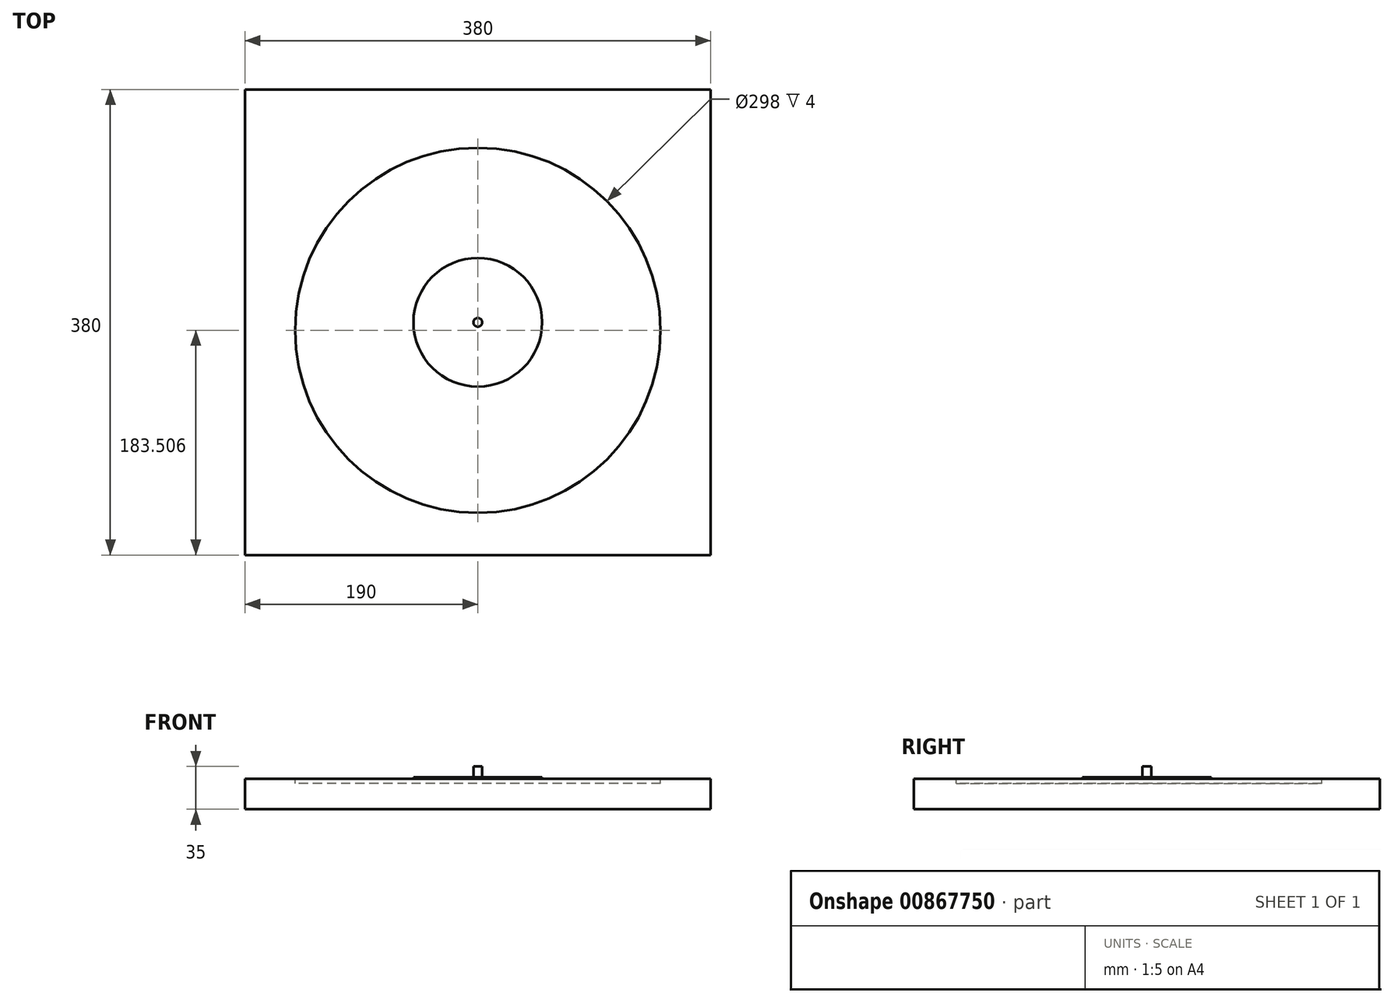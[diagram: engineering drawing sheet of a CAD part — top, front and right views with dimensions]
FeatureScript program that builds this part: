
annotation { "Feature Type Name" : "Feature", "Feature Type Description" : "" }
export const myFeature = defineFeature(function(context is Context, id is Id, definition is map)
    precondition{}
    {
        {
            var Q0;
            Q0=qCreatedBy(makeId("Top.planeOp"),FACE);
            var sketch = newSketch(context, id + "F0", { "sketchPlane" : qUnion([Q0])});
            skLineSegment(sketch, "E0.bottom", {"start": v(-190, 190) * mm, "end": v(190, 190) * mm});
            skLineSegment(sketch, "E0.top", {"start": v(-190, -190) * mm, "end": v(190, -190) * mm});
            skLineSegment(sketch, "E0.left", {"start": v(-190, 190) * mm, "end": v(-190, -190) * mm});
            skLineSegment(sketch, "E0.right", {"start": v(190, 190) * mm, "end": v(190, -190) * mm});
            skPoint(sketch, "E0.middle", {"position": v(0, 0) * mm});
            skSolve(sketch);
        }
        {
            var Q0;
            Q0=makeQuery(id+"F0.imprint","IMPRINT",FACE,{"disambiguationData":[TD([[makeQuery(id+"F0.imprint","IMPRINT",EDGE,{"derivedFrom":sQuery(id+"F0.wireOp",EDGE,"E0.bottom")}),-1.0]])]});
            extrude(context, id + "F1", {"entities" : qUnion([Q0]), "depth" : 25 * mm, "offsetDistance" : 25 * mm});
        }
        {
            var Q0;
            Q0=makeQuery(id+"F1.opExtrude","CAP_FACE",FACE,{"disambiguationData":[OSD([sQuery(id+"F0.wireOp",EDGE,"E0.bottom"),sQuery(id+"F0.wireOp",EDGE,"E0.top"),sQuery(id+"F0.wireOp",EDGE,"E0.left"),sQuery(id+"F0.wireOp",EDGE,"E0.right")])],"isStart":false});
            var sketch = newSketch(context, id + "F2", { "sketchPlane" : qUnion([Q0])});
            skCircle(sketch, "E1", {"center": v(0, -6.5) * mm, "radius": 149 * mm});
            skSolve(sketch);
        }
        {
            var Q0;
            Q0=makeQuery(id+"F2.imprint","IMPRINT",FACE,{"disambiguationData":[TD([[makeQuery(id+"F2.imprint","IMPRINT",EDGE,{"derivedFrom":sQuery(id+"F2.wireOp",EDGE,"E1")}),1.0]])]});
            extrude(context, id + "F3", {"entities" : qUnion([Q0]), "operationType" : NewBodyOperationType.REMOVE, "oppositeDirection" : true, "depth" : 4 * mm, "offsetDistance" : 25 * mm});
        }
        {
            var Q0;
            Q0=makeQuery(id+"F1.opExtrude","CAP_FACE",FACE,{"disambiguationData":[OSD([sQuery(id+"F0.wireOp",EDGE,"E0.bottom"),sQuery(id+"F0.wireOp",EDGE,"E0.top"),sQuery(id+"F0.wireOp",EDGE,"E0.left"),sQuery(id+"F0.wireOp",EDGE,"E0.right")])],"isStart":false});
            var sketch = newSketch(context, id + "F4", { "sketchPlane" : qUnion([Q0])});
            skCircle(sketch, "E2", {"center": v(0, 0) * mm, "radius": 52.5 * mm});
            skSolve(sketch);
        }
        {
            var Q0;
            Q0=makeQuery(id+"F4.imprint","IMPRINT",FACE,{"disambiguationData":[TD([[makeQuery(id+"F4.imprint","IMPRINT",EDGE,{"derivedFrom":sQuery(id+"F4.wireOp",EDGE,"E2")}),1.0]])]});
            extrude(context, id + "F5", {"entities" : qUnion([Q0]), "depth" : 1 * mm, "offsetDistance" : 25 * mm});
        }
        {
            var Q0;
            Q0=makeQuery(id+"F1.opExtrude","CAP_FACE",FACE,{"disambiguationData":[OSD([sQuery(id+"F0.wireOp",EDGE,"E0.bottom"),sQuery(id+"F0.wireOp",EDGE,"E0.top"),sQuery(id+"F0.wireOp",EDGE,"E0.left"),sQuery(id+"F0.wireOp",EDGE,"E0.right")])],"isStart":false});
            var sketch = newSketch(context, id + "F6", { "sketchPlane" : qUnion([Q0])});
            skCircle(sketch, "E3", {"center": v(0, 0) * mm, "radius": 3.6 * mm});
            skSolve(sketch);
        }
        {
            var Q0;
            Q0 = qSketchRegion(id + "F6", true);
            extrude(context, id + "F7", {"entities" : qUnion([Q0]), "operationType" : NewBodyOperationType.ADD, "depth" : 10 * mm, "offsetDistance" : 25 * mm});
        }
    });
